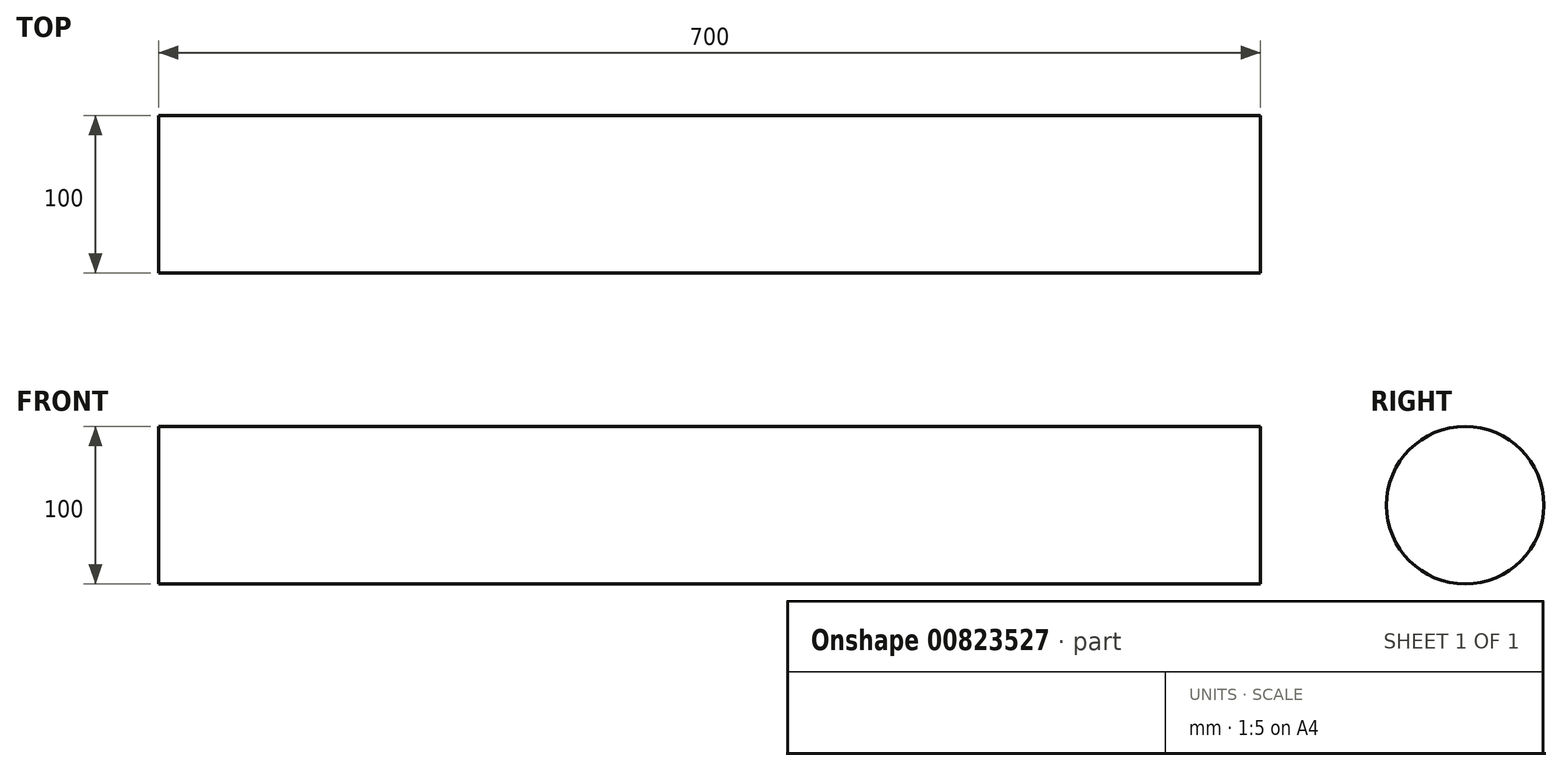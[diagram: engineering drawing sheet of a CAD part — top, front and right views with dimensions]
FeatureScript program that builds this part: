
annotation { "Feature Type Name" : "Feature", "Feature Type Description" : "" }
export const myFeature = defineFeature(function(context is Context, id is Id, definition is map)
    precondition{}
    {
        {
            var Q0;
            Q0=qCreatedBy(makeId("Right.planeOp"),FACE);
            var sketch = newSketch(context, id + "F0", { "sketchPlane" : qUnion([Q0])});
            skCircle(sketch, "E0", {"center": v(0, 0) * mm, "radius": 50 * mm});
            skSolve(sketch);
        }
        {
            var Q0;
            Q0 = qSketchRegion(id + "F0", true);
            extrude(context, id + "F1", {"entities" : qUnion([Q0]), "depth" : 700 * mm, "offsetDistance" : 25 * mm});
        }
    });
